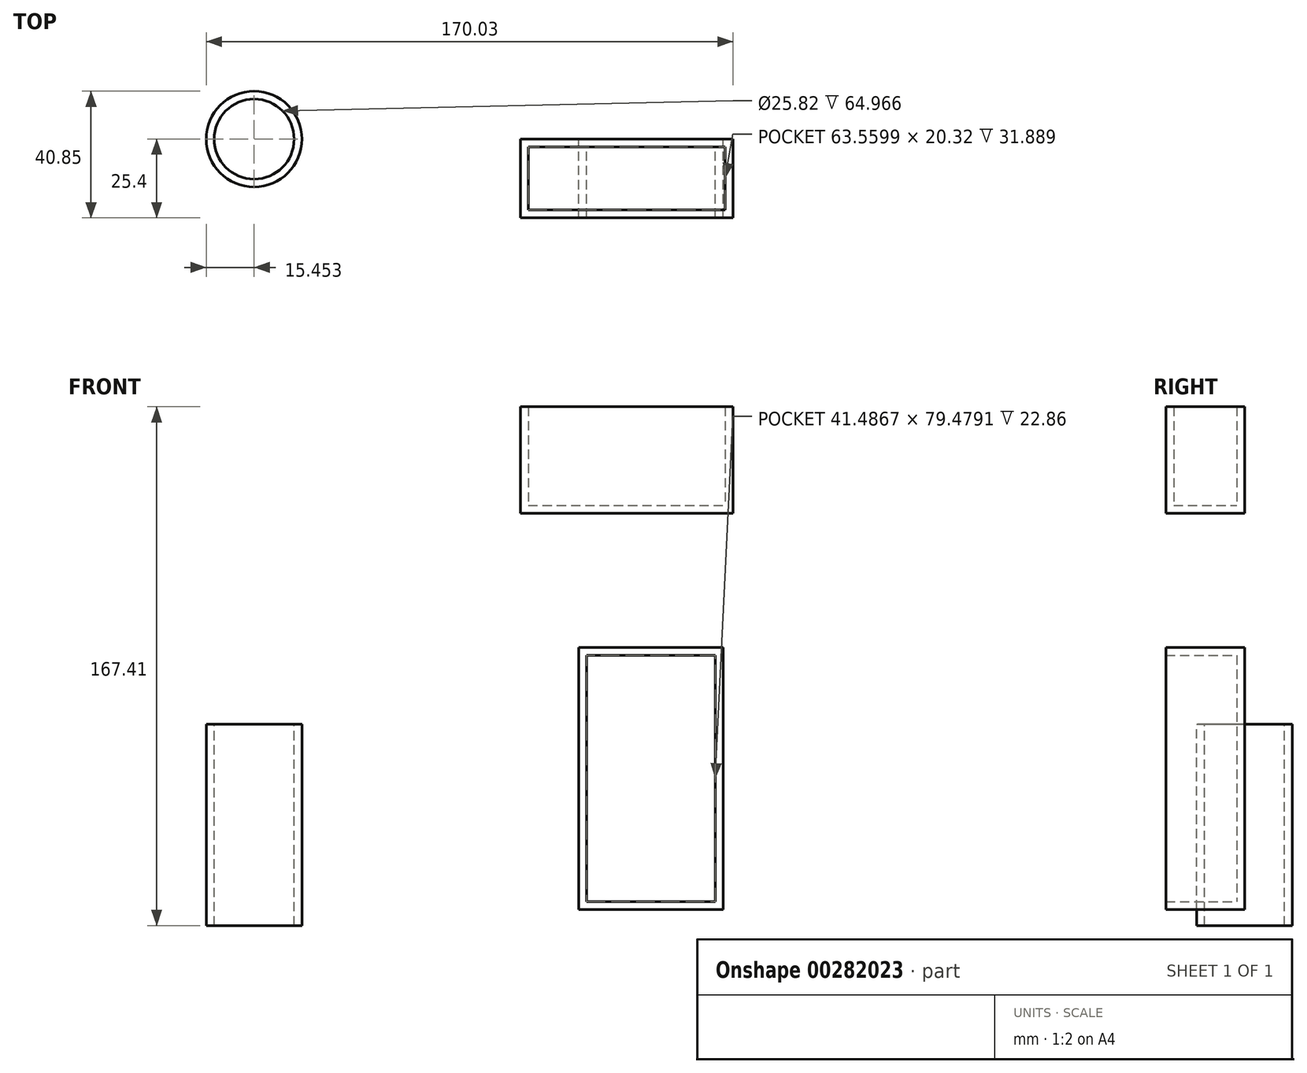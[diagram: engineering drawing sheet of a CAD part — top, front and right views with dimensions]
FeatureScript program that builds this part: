
annotation { "Feature Type Name" : "Feature", "Feature Type Description" : "" }
export const myFeature = defineFeature(function(context is Context, id is Id, definition is map)
    precondition{}
    {
        {
            var Q0;
            Q0=qCreatedBy(makeId("Front.planeOp"),FACE);
            var sketch = newSketch(context, id + "F3", { "sketchPlane" : qUnion([Q0])});
            skLineSegment(sketch, "E0.bottom", {"start": v(0, 154.05) * mm, "end": v(68.64, 154.05) * mm});
            skLineSegment(sketch, "E0.top", {"start": v(0, 119.63) * mm, "end": v(68.64, 119.63) * mm});
            skLineSegment(sketch, "E0.left", {"start": v(0, 154.05) * mm, "end": v(0, 119.63) * mm});
            skLineSegment(sketch, "E0.right", {"start": v(68.64, 154.05) * mm, "end": v(68.64, 119.63) * mm});
            skLineSegment(sketch, "E1.bottom", {"start": v(-85.94, 51.6) * mm, "end": v(-70.49, 51.6) * mm});
            skLineSegment(sketch, "E1.top", {"start": v(-85.94, -13.36) * mm, "end": v(-70.49, -13.36) * mm});
            skLineSegment(sketch, "E1.left", {"start": v(-85.94, 51.6) * mm, "end": v(-85.94, -13.36) * mm});
            skLineSegment(sketch, "E1.right", {"start": v(-70.49, 51.6) * mm, "end": v(-70.49, -13.36) * mm});
            skLineSegment(sketch, "E2.bottom", {"start": v(18.84, 76.35) * mm, "end": v(65.4, 76.35) * mm});
            skLineSegment(sketch, "E2.top", {"start": v(18.84, -8.21) * mm, "end": v(65.4, -8.21) * mm});
            skLineSegment(sketch, "E2.left", {"start": v(18.84, 76.35) * mm, "end": v(18.84, -8.21) * mm});
            skLineSegment(sketch, "E2.right", {"start": v(65.4, 76.35) * mm, "end": v(65.4, -8.21) * mm});
            skLineSegment(sketch, "E3.bottom", {"start": v(-75.78, -69.08) * mm, "end": v(28.97, -69.08) * mm});
            skLineSegment(sketch, "E3.top", {"start": v(-75.78, -98.5) * mm, "end": v(28.97, -98.5) * mm});
            skLineSegment(sketch, "E3.left", {"start": v(-75.78, -69.08) * mm, "end": v(-75.78, -98.5) * mm});
            skLineSegment(sketch, "E3.right", {"start": v(28.97, -69.08) * mm, "end": v(28.97, -98.5) * mm});
            skSolve(sketch);
        }
        {
            var Q0;
            Q0 = qSketchRegion(id + "F3", true);
            extrude(context, id + "F0", {"entities" : qUnion([Q0]), "depth" : 25.4 * mm});
        }
        {
            var Q0;
            Q0=makeQuery(id+"F0.opExtrude","SWEPT_BODY",BODY,{"disambiguationData":[OSD([sQuery(id+"F3.wireOp",EDGE,"E3.bottom"),sQuery(id+"F3.wireOp",EDGE,"E3.top"),sQuery(id+"F3.wireOp",EDGE,"E3.left"),sQuery(id+"F3.wireOp",EDGE,"E3.right")])]});
            var Q1;
            Q1=makeQuery(id+"F0.opExtrude","SWEPT_BODY",BODY,{"disambiguationData":[OSD([sQuery(id+"F3.wireOp",EDGE,"E1.bottom"),sQuery(id+"F3.wireOp",EDGE,"E1.top"),sQuery(id+"F3.wireOp",EDGE,"E1.left"),sQuery(id+"F3.wireOp",EDGE,"E1.right")])]});
            deleteBodies(context, id + "F1", {"entities" : qUnion([Q0, Q1])});
        }
        {
            var Q0;
            Q0=makeQuery(id+"F3.imprint","IMPRINT",FACE,{"disambiguationData":[TD([[makeQuery(id+"F3.imprint","IMPRINT",EDGE,{"derivedFrom":sQuery(id+"F3.wireOp",EDGE,"E1.bottom")}),-1.0]])]});
            var Q1;
            Q1=sQuery(id+"F3.wireOp",EDGE,"E1.left");
            revolve(context, id + "F4", {"entities" : qUnion([Q0]), "axis" : qUnion([Q1]), "revolveType" : RevolveType.FULL});
        }
        {
            var Q0;
            Q0=makeQuery(id+"F4.opRevolve","SWEPT_FACE",FACE,{"disambiguationData":[OSD([sQuery(id+"F3.wireOp",EDGE,"E1.bottom")])]});
            var Q1;
            Q1=makeQuery(id+"F4.opRevolve","SWEPT_FACE",FACE,{"disambiguationData":[OSD([sQuery(id+"F3.wireOp",EDGE,"E1.top")])]});
            var Q2;
            Q2=makeQuery(id+"F0.opExtrude","CAP_FACE",FACE,{"disambiguationData":[OSD([sQuery(id+"F3.wireOp",EDGE,"E2.bottom"),sQuery(id+"F3.wireOp",EDGE,"E2.top"),sQuery(id+"F3.wireOp",EDGE,"E2.left"),sQuery(id+"F3.wireOp",EDGE,"E2.right")])],"isStart":false});
            var Q3;
            Q3=makeQuery(id+"F0.opExtrude","SWEPT_FACE",FACE,{"disambiguationData":[OSD([sQuery(id+"F3.wireOp",EDGE,"E0.bottom")])]});
            shell(context, id + "F2", {"entities" : qUnion([Q0, Q1, Q2, Q3]), "thickness" : 2.54 * mm});
        }
    });
